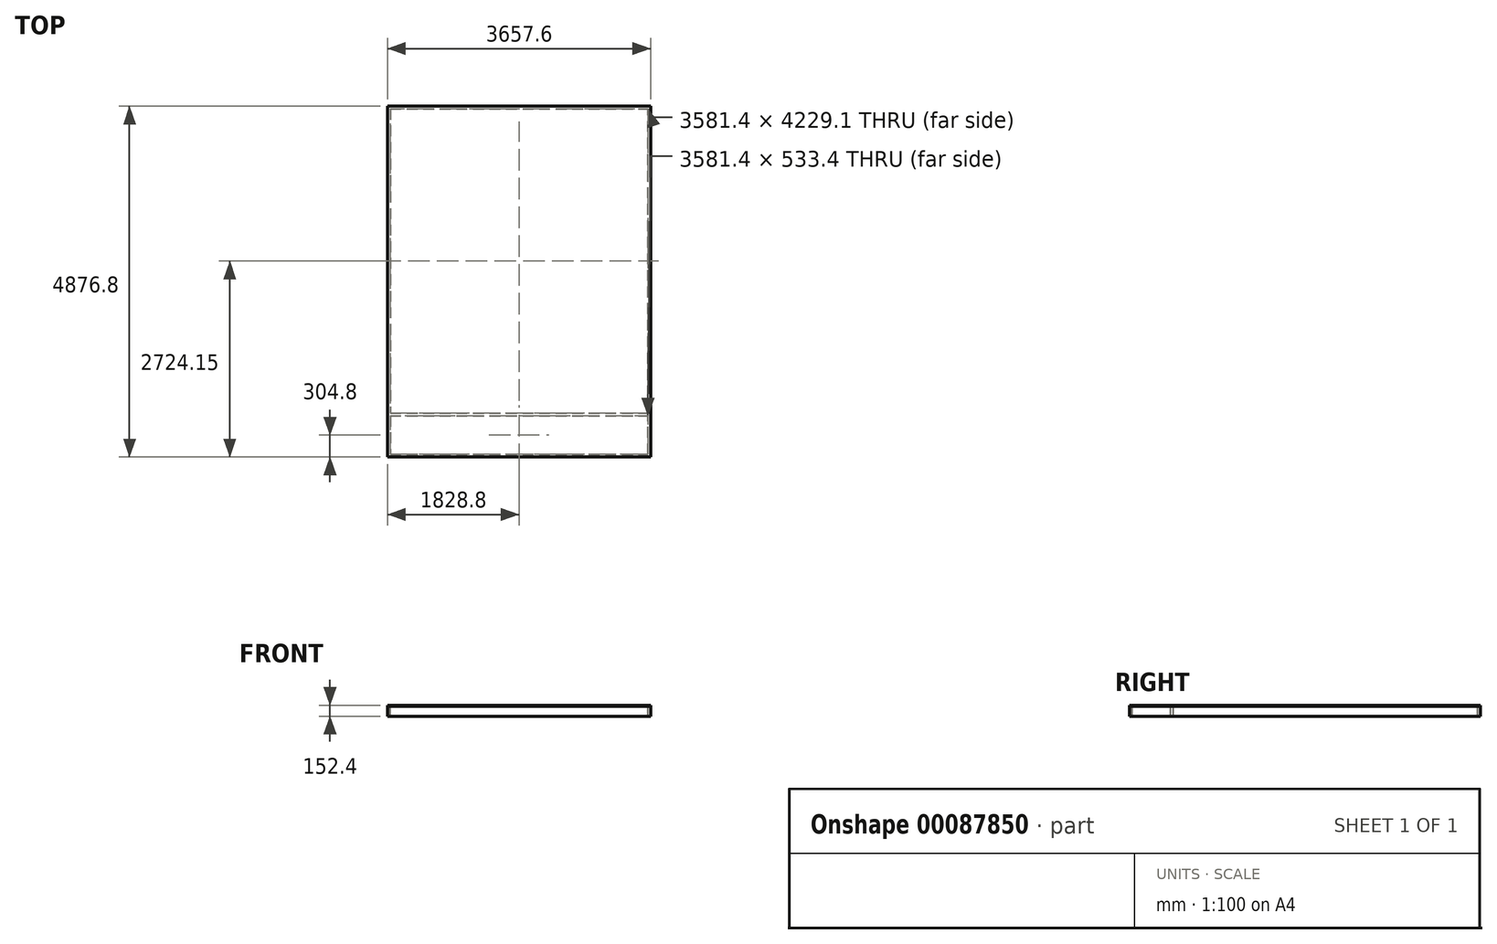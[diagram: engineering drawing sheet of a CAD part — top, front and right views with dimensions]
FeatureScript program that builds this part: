
annotation { "Feature Type Name" : "Feature", "Feature Type Description" : "" }
export const myFeature = defineFeature(function(context is Context, id is Id, definition is map)
    precondition{}
    {
        {
            var Q0;
            Q0=qCreatedBy(makeId("Top.planeOp"),FACE);
            var sketch = newSketch(context, id + "F0", { "sketchPlane" : qUnion([Q0])});
            skLineSegment(sketch, "E0.bottom", {"start": v(-1790.7, 2438.4) * mm, "end": v(1790.7, 2438.4) * mm});
            skLineSegment(sketch, "E0.top", {"start": v(-1790.7, 2400.3) * mm, "end": v(1790.7, 2400.3) * mm});
            skLineSegment(sketch, "E0.left", {"start": v(-1790.7, 2438.4) * mm, "end": v(-1790.7, 2400.3) * mm});
            skLineSegment(sketch, "E0.right", {"start": v(1790.7, 2438.4) * mm, "end": v(1790.7, 2400.3) * mm});
            skLineSegment(sketch, "E1.bottom", {"start": v(-1790.7, 2438.4) * mm, "end": v(-1828.8, 2438.4) * mm});
            skLineSegment(sketch, "E1.top", {"start": v(-1790.7, -2438.4) * mm, "end": v(-1828.8, -2438.4) * mm});
            skLineSegment(sketch, "E1.left", {"start": v(-1790.7, 2438.4) * mm, "end": v(-1790.7, -2438.4) * mm});
            skLineSegment(sketch, "E1.right", {"start": v(-1828.8, 2438.4) * mm, "end": v(-1828.8, -2438.4) * mm});
            skLineSegment(sketch, "E2.bottom", {"start": v(-1790.7, -2438.4) * mm, "end": v(1790.7, -2438.4) * mm});
            skLineSegment(sketch, "E2.top", {"start": v(-1790.7, -2400.3) * mm, "end": v(1790.7, -2400.3) * mm});
            skLineSegment(sketch, "E2.left", {"start": v(-1790.7, -2438.4) * mm, "end": v(-1790.7, -2400.3) * mm});
            skLineSegment(sketch, "E2.right", {"start": v(1790.7, -2438.4) * mm, "end": v(1790.7, -2400.3) * mm});
            skLineSegment(sketch, "E3.bottom", {"start": v(1790.7, -2438.4) * mm, "end": v(1828.8, -2438.4) * mm});
            skLineSegment(sketch, "E3.top", {"start": v(1790.7, 2438.4) * mm, "end": v(1828.8, 2438.4) * mm});
            skLineSegment(sketch, "E3.left", {"start": v(1790.7, -2438.4) * mm, "end": v(1790.7, 2438.4) * mm});
            skLineSegment(sketch, "E3.right", {"start": v(1828.8, -2438.4) * mm, "end": v(1828.8, 2438.4) * mm});
            skPoint(sketch, "E4", {"position": v(0, 2438.4) * mm});
            skPoint(sketch, "E5", {"position": v(1790.7, 0) * mm});
            skLineSegment(sketch, "E6.bottom", {"start": v(-1790.7, -1866.9) * mm, "end": v(1790.7, -1866.9) * mm});
            skLineSegment(sketch, "E6.top", {"start": v(-1790.7, -1828.8) * mm, "end": v(1790.7, -1828.8) * mm});
            skLineSegment(sketch, "E6.left", {"start": v(-1790.7, -1866.9) * mm, "end": v(-1790.7, -1828.8) * mm});
            skLineSegment(sketch, "E6.right", {"start": v(1790.7, -1866.9) * mm, "end": v(1790.7, -1828.8) * mm});
            skLineSegment(sketch, "E7.0.1.0", {"start": v(-1790.7, -1257.3) * mm, "end": v(-1790.7, -1219.2) * mm});
            skLineSegment(sketch, "E7.0.1.1", {"start": v(-1790.7, -1257.3) * mm, "end": v(1790.7, -1257.3) * mm});
            skLineSegment(sketch, "E7.0.1.2", {"start": v(-1790.7, -1219.2) * mm, "end": v(1790.7, -1219.2) * mm});
            skLineSegment(sketch, "E7.0.1.3", {"start": v(1790.7, -1257.3) * mm, "end": v(1790.7, -1219.2) * mm});
            skLineSegment(sketch, "E7.0.2.0", {"start": v(-1790.7, -647.7) * mm, "end": v(-1790.7, -609.6) * mm});
            skLineSegment(sketch, "E7.0.2.1", {"start": v(-1790.7, -647.7) * mm, "end": v(1790.7, -647.7) * mm});
            skLineSegment(sketch, "E7.0.2.2", {"start": v(-1790.7, -609.6) * mm, "end": v(1790.7, -609.6) * mm});
            skLineSegment(sketch, "E7.0.2.3", {"start": v(1790.7, -647.7) * mm, "end": v(1790.7, -609.6) * mm});
            skLineSegment(sketch, "E7.0.3.0", {"start": v(-1790.7, -38.1) * mm, "end": v(-1790.7, 0) * mm});
            skLineSegment(sketch, "E7.0.3.1", {"start": v(-1790.7, -38.1) * mm, "end": v(1790.7, -38.1) * mm});
            skLineSegment(sketch, "E7.0.3.2", {"start": v(-1790.7, 0) * mm, "end": v(1790.7, 0) * mm});
            skLineSegment(sketch, "E7.0.3.3", {"start": v(1790.7, -38.1) * mm, "end": v(1790.7, 0) * mm});
            skLineSegment(sketch, "E7.0.4.0", {"start": v(-1790.7, 571.5) * mm, "end": v(-1790.7, 609.6) * mm});
            skLineSegment(sketch, "E7.0.4.1", {"start": v(-1790.7, 571.5) * mm, "end": v(1790.7, 571.5) * mm});
            skLineSegment(sketch, "E7.0.4.2", {"start": v(-1790.7, 609.6) * mm, "end": v(1790.7, 609.6) * mm});
            skLineSegment(sketch, "E7.0.4.3", {"start": v(1790.7, 571.5) * mm, "end": v(1790.7, 609.6) * mm});
            skLineSegment(sketch, "E7.0.5.0", {"start": v(-1790.7, 1181.1) * mm, "end": v(-1790.7, 1219.2) * mm});
            skLineSegment(sketch, "E7.0.5.1", {"start": v(-1790.7, 1181.1) * mm, "end": v(1790.7, 1181.1) * mm});
            skLineSegment(sketch, "E7.0.5.2", {"start": v(-1790.7, 1219.2) * mm, "end": v(1790.7, 1219.2) * mm});
            skLineSegment(sketch, "E7.0.5.3", {"start": v(1790.7, 1181.1) * mm, "end": v(1790.7, 1219.2) * mm});
            skLineSegment(sketch, "E7.0.6.0", {"start": v(-1790.7, 1790.7) * mm, "end": v(-1790.7, 1828.8) * mm});
            skLineSegment(sketch, "E7.0.6.1", {"start": v(-1790.7, 1790.7) * mm, "end": v(1790.7, 1790.7) * mm});
            skLineSegment(sketch, "E7.0.6.2", {"start": v(-1790.7, 1828.8) * mm, "end": v(1790.7, 1828.8) * mm});
            skLineSegment(sketch, "E7.0.6.3", {"start": v(1790.7, 1790.7) * mm, "end": v(1790.7, 1828.8) * mm});
            skLineSegment(sketch, "E7.direction1", {"start": v(-1790.7, -1866.9) * mm, "end": v(-1765.7, -1866.9) * mm, "construction": true});
            skLineSegment(sketch, "E7.direction2", {"start": v(-1790.7, -1866.9) * mm, "end": v(-1790.7, -1257.3) * mm, "construction": true});
            skSolve(sketch);
        }
        {
            var Q0;
            Q0 = qSketchRegion(id + "F0", true);
            var Q1;
            Q1=makeQuery(id+"F0.imprint","IMPRINT",FACE,{"disambiguationData":[TD([[makeQuery(id+"F0.imprint","IMPRINT",EDGE,{"derivedFrom":sQuery(id+"F0.wireOp",EDGE,"E6.bottom")}),1.0]])]});
            var Q2;
            Q2=makeQuery(id+"F0.imprint","IMPRINT",FACE,{"disambiguationData":[TD([[makeQuery(id+"F0.imprint","IMPRINT",EDGE,{"derivedFrom":sQuery(id+"F0.wireOp",EDGE,"E7.0.1.0")}),-1.0]])]});
            var Q3;
            Q3=makeQuery(id+"F0.imprint","IMPRINT",FACE,{"disambiguationData":[TD([[makeQuery(id+"F0.imprint","IMPRINT",EDGE,{"derivedFrom":sQuery(id+"F0.wireOp",EDGE,"E7.0.2.0")}),-1.0]])]});
            var Q4;
            Q4=makeQuery(id+"F0.imprint","IMPRINT",FACE,{"disambiguationData":[TD([[makeQuery(id+"F0.imprint","IMPRINT",EDGE,{"derivedFrom":sQuery(id+"F0.wireOp",EDGE,"E7.0.3.0")}),-1.0]])]});
            var Q5;
            Q5=makeQuery(id+"F0.imprint","IMPRINT",FACE,{"disambiguationData":[TD([[makeQuery(id+"F0.imprint","IMPRINT",EDGE,{"derivedFrom":sQuery(id+"F0.wireOp",EDGE,"E7.0.4.0")}),-1.0]])]});
            var Q6;
            Q6=makeQuery(id+"F0.imprint","IMPRINT",FACE,{"disambiguationData":[TD([[makeQuery(id+"F0.imprint","IMPRINT",EDGE,{"derivedFrom":sQuery(id+"F0.wireOp",EDGE,"E7.0.5.0")}),-1.0]])]});
            var Q7;
            Q7=makeQuery(id+"F0.imprint","IMPRINT",FACE,{"disambiguationData":[TD([[makeQuery(id+"F0.imprint","IMPRINT",EDGE,{"derivedFrom":sQuery(id+"F0.wireOp",EDGE,"E7.0.6.0")}),-1.0]])]});
            extrude(context, id + "F1", {"entities" : qUnion([Q0, Q1, Q2, Q3, Q4, Q5, Q6, Q7]), "oppositeDirection" : true, "depth" : 139.7 * mm});
        }
        {
            var Q0;
            Q0=qCreatedBy(makeId("Top.planeOp"),FACE);
            var sketch = newSketch(context, id + "F2", { "sketchPlane" : qUnion([Q0])});
            skLineSegment(sketch, "E8.0", {"start": v(-1828.8, 2438.4) * mm, "end": v(-1828.8, -2438.4) * mm});
            skLineSegment(sketch, "E8.1", {"start": v(-1828.8, 2438.4) * mm, "end": v(1828.8, 2438.4) * mm});
            skLineSegment(sketch, "E8.2", {"start": v(1828.8, -2438.4) * mm, "end": v(1828.8, 2438.4) * mm});
            skLineSegment(sketch, "E8.3", {"start": v(-1828.8, -2438.4) * mm, "end": v(1828.8, -2438.4) * mm});
            skSolve(sketch);
        }
        {
            var Q0;
            Q0 = qSketchRegion(id + "F2", true);
            extrude(context, id + "F3", {"entities" : qUnion([Q0]), "depth" : 12.7 * mm});
        }
    });
